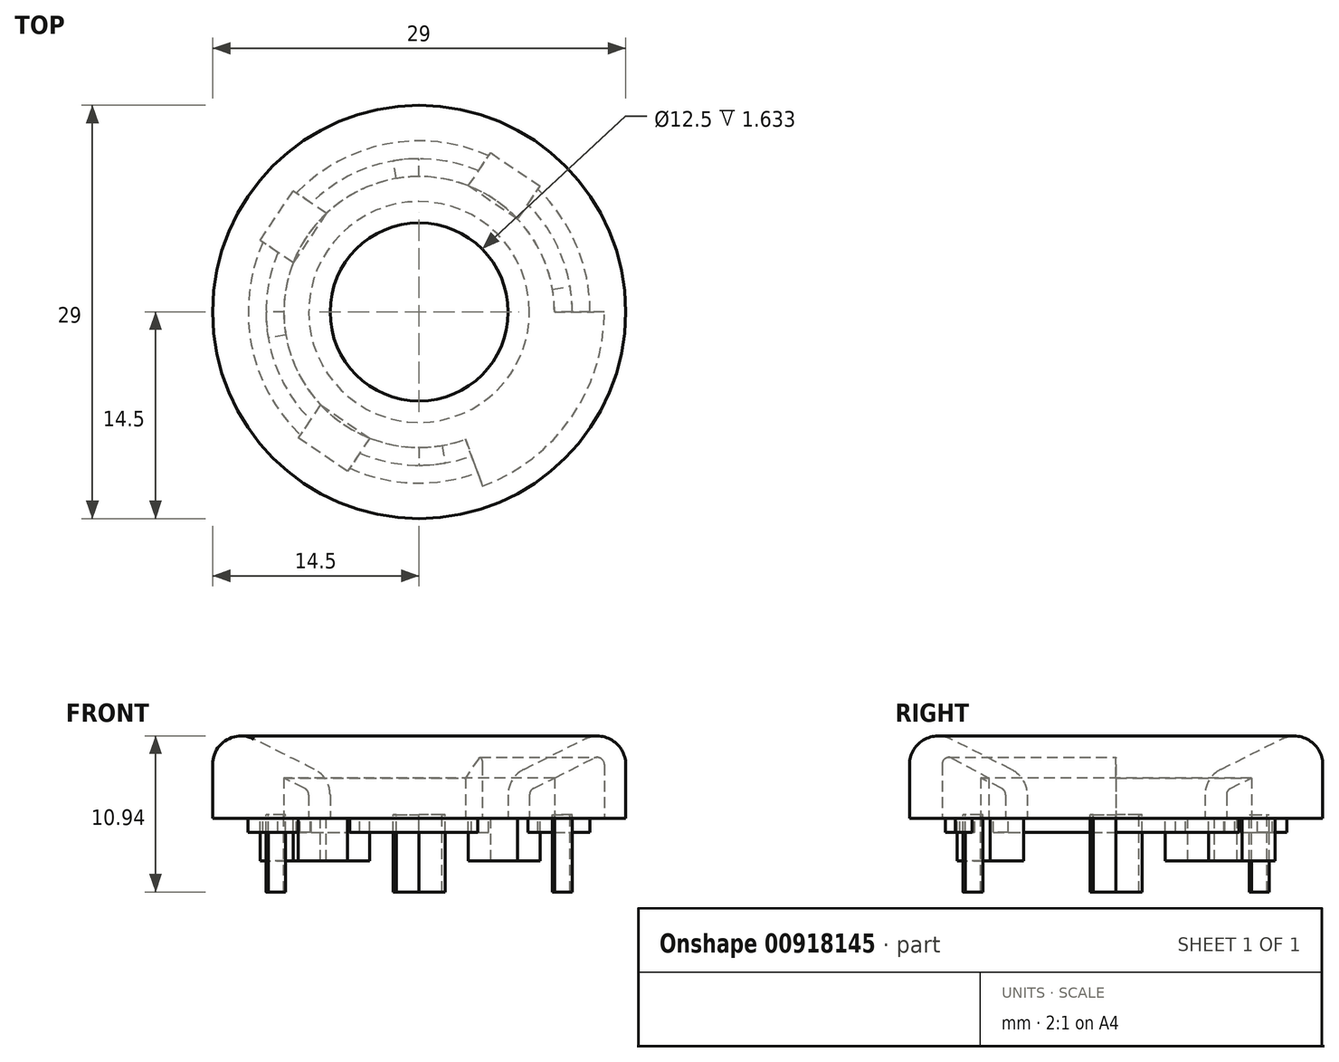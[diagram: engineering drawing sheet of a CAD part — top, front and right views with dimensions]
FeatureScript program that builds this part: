
annotation { "Feature Type Name" : "Feature", "Feature Type Description" : "" }
export const myFeature = defineFeature(function(context is Context, id is Id, definition is map)
    precondition{}
    {
        {
            var Q0;
            Q0=qCreatedBy(makeId("Front.planeOp"),FACE);
            var sketch = newSketch(context, id + "F0", { "sketchPlane" : qUnion([Q0])});
            skLineSegment(sketch, "E0", {"start": v(-6.25, 0) * mm, "end": v(-14.5, 0) * mm});
            skLineSegment(sketch, "E1", {"start": v(-14.5, 0) * mm, "end": v(-14.5, 3.76) * mm});
            skLineSegment(sketch, "E2", {"start": v(-6.25, 1.63) * mm, "end": v(-6.25, 0) * mm});
            skPoint(sketch, "E3.visualSharp", {"position": v(-14.5, 7) * mm});
            skPoint(sketch, "E4.orphan", {"position": v(0, 0) * mm});
            skPoint(sketch, "E5.visualSharp", {"position": v(-6.25, 2.47) * mm});
            skArc(sketch, "E5.filletArc", {"start": v(-6.25, 1.63) * mm, "mid": v(-6.55, 2.68) * mm, "end": v(-7.35, 3.42) * mm});
            skLineSegment(sketch, "E6", {"start": v(0, 0) * mm, "end": v(0, 11.37) * mm, "construction": true});
            skLineSegment(sketch, "E7", {"start": v(-7.35, 3.42) * mm, "end": v(-11.6, 5.55) * mm});
            skPoint(sketch, "E8.orphan", {"position": v(-14.5, 7.63) * mm});
            skArc(sketch, "E9.filletArc", {"start": v(-11.6, 5.55) * mm, "mid": v(-13.55, 5.46) * mm, "end": v(-14.5, 3.76) * mm});
            skSolve(sketch);
        }
        {
            var Q0;
            Q0=makeQuery(id+"F0.imprint","IMPRINT",FACE,{"disambiguationData":[TD([[makeQuery(id+"F0.imprint","IMPRINT",EDGE,{"derivedFrom":sQuery(id+"F0.wireOp",EDGE,"E0")}),-1.0]])]});
            var Q1;
            Q1=sQuery(id+"F0.wireOp",EDGE,"E6");
            revolve(context, id + "F1", {"surfaceOperationType" : NewSurfaceOperationType.NEW, "entities" : qUnion([Q0]), "axis" : qUnion([Q1]), "revolveType" : RevolveType.FULL});
        }
        {
            var Q0;
            Q0=makeQuery(id+"F1.opRevolve","SWEPT_FACE",FACE,{"disambiguationData":[OSD([sQuery(id+"F0.wireOp",EDGE,"E0")])]});
            shell(context, id + "F2", {"entities" : qUnion([Q0]), "thickness" : 1.5 * mm});
        }
        {
            var Q0;
            Q0=makeQuery(id+"F1.opRevolve","SWEPT_FACE",FACE,{"disambiguationData":[OSD([sQuery(id+"F0.wireOp",EDGE,"E0")])]});
            var sketch = newSketch(context, id + "F3", { "sketchPlane" : qUnion([Q0])});
            skLineSegment(sketch, "E10", {"start": v(13, 0) * mm, "end": v(9.5, 0) * mm});
            skArc(sketch, "E11", {"start": v(3.25, 8.93) * mm, "mid": v(-7.78, -5.45) * mm, "end": v(9.5, 0) * mm});
            skArc(sketch, "E12", {"start": v(4.45, 12.22) * mm, "mid": v(-10.65, -7.46) * mm, "end": v(13, 0) * mm});
            skLineSegment(sketch, "E13", {"start": v(3.25, 8.93) * mm, "end": v(4.45, 12.22) * mm});
            skPoint(sketch, "E14.orphan", {"position": v(0, 9.5) * mm});
            skSolve(sketch);
        }
        {
            var Q0;
            Q0=makeQuery(id+"F3.imprint","IMPRINT",FACE,{"disambiguationData":[TD([[makeQuery(id+"F3.imprint","IMPRINT",EDGE,{"derivedFrom":sQuery(id+"F3.wireOp",EDGE,"E10")}),1.0]])]});
            extrude(context, id + "F4", {"entities" : qUnion([Q0]), "operationType" : NewBodyOperationType.ADD, "endBound" : BoundingType.UP_TO_NEXT, "oppositeDirection" : true, "depth" : 25 * mm, "offsetDistance" : 25 * mm});
        }
        {
            var Q0;
            Q0=makeQuery(id+"F4.boolean.opBoolean","MERGE",FACE,{"derivedFrom":[makeQuery(id+"F1.opRevolve","SWEPT_FACE",FACE,{"disambiguationData":[OSD([sQuery(id+"F0.wireOp",EDGE,"E0")])]}),makeQuery(id+"F4.opExtrude","CAP_FACE",FACE,{"disambiguationData":[OSD([sQuery(id+"F3.wireOp",EDGE,"E10"),sQuery(id+"F3.wireOp",EDGE,"E11"),sQuery(id+"F3.wireOp",EDGE,"E12"),sQuery(id+"F3.wireOp",EDGE,"E13")])],"isStart":true})]});
            var sketch = newSketch(context, id + "F5", { "sketchPlane" : qUnion([Q0])});
            skLineSegment(sketch, "E15", {"start": v(6.92, -6.5) * mm, "end": v(3.46, -8.85) * mm});
            skLineSegment(sketch, "E16", {"start": v(3.46, -8.85) * mm, "end": v(5.03, -11.17) * mm});
            skLineSegment(sketch, "E17", {"start": v(5.03, -11.17) * mm, "end": v(8.49, -8.83) * mm});
            skLineSegment(sketch, "E18", {"start": v(6.92, -6.5) * mm, "end": v(8.49, -8.83) * mm});
            skLineSegment(sketch, "E19.1.0", {"start": v(-6.5, -6.92) * mm, "end": v(-8.83, -8.49) * mm});
            skLineSegment(sketch, "E19.1.1", {"start": v(-6.5, -6.92) * mm, "end": v(-8.85, -3.46) * mm});
            skLineSegment(sketch, "E19.1.2", {"start": v(-11.17, -5.03) * mm, "end": v(-8.83, -8.49) * mm});
            skLineSegment(sketch, "E19.1.3", {"start": v(-8.85, -3.46) * mm, "end": v(-11.17, -5.03) * mm});
            skLineSegment(sketch, "E19.2.0", {"start": v(-6.92, 6.5) * mm, "end": v(-8.49, 8.83) * mm});
            skLineSegment(sketch, "E19.2.1", {"start": v(-6.92, 6.5) * mm, "end": v(-3.46, 8.85) * mm});
            skLineSegment(sketch, "E19.2.2", {"start": v(-5.03, 11.17) * mm, "end": v(-8.49, 8.83) * mm});
            skLineSegment(sketch, "E19.2.3", {"start": v(-3.46, 8.85) * mm, "end": v(-5.03, 11.17) * mm});
            skPoint(sketch, "E19.center", {"position": v(0, 0) * mm});
            skLineSegment(sketch, "E19.anchor1", {"start": v(0, 0) * mm, "end": v(5.03, -11.17) * mm, "construction": true});
            skLineSegment(sketch, "E19.anchor2", {"start": v(0, 0) * mm, "end": v(-5.03, 11.17) * mm, "construction": true});
            skSolve(sketch);
        }
        {
            var Q0;
            {var subQ0=sQuery(id+"F5.wireOp",EDGE,"E19.2.0");Q0=makeQuery(id+"F5.imprint","IMPRINT",FACE,{"disambiguationData":[TD([[makeQuery(id+"F5.imprint","IMPRINT",EDGE,{"derivedFrom":subQ0}),-1.0]])]});}
            var Q1;
            {var subQ0=sQuery(id+"F5.wireOp",EDGE,"E19.1.0");Q1=makeQuery(id+"F5.imprint","IMPRINT",FACE,{"disambiguationData":[TD([[makeQuery(id+"F5.imprint","IMPRINT",EDGE,{"derivedFrom":subQ0}),-1.0]])]});}
            var Q2;
            {var subQ0=sQuery(id+"F5.wireOp",EDGE,"E16");Q2=makeQuery(id+"F5.imprint","IMPRINT",FACE,{"disambiguationData":[TD([[makeQuery(id+"F5.imprint","IMPRINT",EDGE,{"derivedFrom":subQ0}),1.0]])]});}
            var Q3;
            {var subQ0=sQuery(id+"F5.wireOp",EDGE,"E15");Q3=makeQuery(id+"F5.imprint","IMPRINT",FACE,{"disambiguationData":[TD([[makeQuery(id+"F5.imprint","IMPRINT",EDGE,{"derivedFrom":subQ0}),1.0]])]});}
            var Q4;
            {var subQ0=sQuery(id+"F5.wireOp",EDGE,"E19.1.1");Q4=makeQuery(id+"F5.imprint","IMPRINT",FACE,{"disambiguationData":[TD([[makeQuery(id+"F5.imprint","IMPRINT",EDGE,{"derivedFrom":subQ0}),1.0]])]});}
            var Q5;
            {var subQ0=sQuery(id+"F5.wireOp",EDGE,"E19.2.1");Q5=makeQuery(id+"F5.imprint","IMPRINT",FACE,{"disambiguationData":[TD([[makeQuery(id+"F5.imprint","IMPRINT",EDGE,{"derivedFrom":subQ0}),1.0]])]});}
            extrude(context, id + "F6", {"entities" : qUnion([Q0, Q1, Q2, Q3, Q4, Q5]), "operationType" : NewBodyOperationType.ADD, "depth" : 3 * mm, "offsetDistance" : 25 * mm});
        }
        {
            var Q0;
            Q0=makeQuery(id+"F4.boolean.opBoolean","MERGE",FACE,{"derivedFrom":[makeQuery(id+"F1.opRevolve","SWEPT_FACE",FACE,{"disambiguationData":[OSD([sQuery(id+"F0.wireOp",EDGE,"E0")])]}),makeQuery(id+"F4.opExtrude","CAP_FACE",FACE,{"disambiguationData":[OSD([sQuery(id+"F3.wireOp",EDGE,"E10"),sQuery(id+"F3.wireOp",EDGE,"E11"),sQuery(id+"F3.wireOp",EDGE,"E12"),sQuery(id+"F3.wireOp",EDGE,"E13")])],"isStart":true})]});
            var sketch = newSketch(context, id + "F7", { "sketchPlane" : qUnion([Q0])});
            skArc(sketch, "E20", {"start": v(4.1, 11.28) * mm, "mid": v(-9.83, -6.88) * mm, "end": v(12, 0) * mm});
            skArc(sketch, "E21", {"start": v(3.68, 10.1) * mm, "mid": v(-8.8, -6.17) * mm, "end": v(10.75, 0) * mm});
            skLineSegment(sketch, "E22", {"start": v(3.68, 10.1) * mm, "end": v(4.1, 11.28) * mm});
            skLineSegment(sketch, "E23", {"start": v(9.5, 0) * mm, "end": v(12, 0) * mm});
            skSolve(sketch);
        }
        {
            var Q0;
            Q0 = qSketchRegion(id + "F7", true);
            extrude(context, id + "F8", {"entities" : qUnion([Q0]), "operationType" : NewBodyOperationType.ADD, "depth" : 1 * mm, "offsetDistance" : 25 * mm});
        }
        {
            var Q0;
            {var subQ0=sQuery(id+"F5.wireOp",EDGE,"E15");var subQ1=sQuery(id+"F3.wireOp",EDGE,"E11");var subQ2=sQuery(id+"F5.wireOp",EDGE,"E18");var subQ3=sQuery(id+"F3.wireOp",EDGE,"E10");Q0=makeQuery(id+"F8.boolean.opBoolean","SPLIT",FACE,{"disambiguationData":[TD([makeQuery(id+"F4.opExtrude","SWEPT_FACE",FACE,{"disambiguationData":[OSD([subQ3])]}),makeQuery(id+"F4.opExtrude","SWEPT_FACE",FACE,{"disambiguationData":[OSD([subQ1])]}),makeQuery(id+"F6.opExtrude","SWEPT_FACE",FACE,{"disambiguationData":[OSD([subQ0])]}),makeQuery(id+"F6.opExtrude","CAP_FACE",FACE,{"disambiguationData":[OSD([subQ0,sQuery(id+"F5.wireOp",EDGE,"E16"),sQuery(id+"F5.wireOp",EDGE,"E17"),subQ2])],"isStart":true}),makeQuery(id+"F6.opExtrude","SWEPT_FACE",FACE,{"disambiguationData":[OSD([subQ2])]}),makeQuery(id+"F8.opExtrude","SWEPT_FACE",FACE,{"disambiguationData":[OSD([sQuery(id+"F7.wireOp",EDGE,"E21")])]}),makeQuery(id+"F8.opExtrude","SWEPT_FACE",FACE,{"disambiguationData":[OSD([sQuery(id+"F7.wireOp",EDGE,"E23")])]})])],"derivedFrom":makeQuery(id+"F4.boolean.opBoolean","MERGE",FACE,{"derivedFrom":[makeQuery(id+"F1.opRevolve","SWEPT_FACE",FACE,{"disambiguationData":[OSD([sQuery(id+"F0.wireOp",EDGE,"E0")])]}),makeQuery(id+"F4.opExtrude","CAP_FACE",FACE,{"disambiguationData":[OSD([subQ3,subQ1,sQuery(id+"F3.wireOp",EDGE,"E12"),sQuery(id+"F3.wireOp",EDGE,"E13")])],"isStart":true})]})});}
            var sketch = newSketch(context, id + "F9", { "sketchPlane" : qUnion([Q0])});
            skLineSegment(sketch, "E24", {"start": v(9.5, 0) * mm, "end": v(10.75, 0) * mm});
            skLineSegment(sketch, "E25", {"start": v(9.36, -1.6) * mm, "end": v(10.6, -1.81) * mm});
            skArc(sketch, "E26", {"start": v(9.5, 0) * mm, "mid": v(9.47, -0.8) * mm, "end": v(9.36, -1.6) * mm});
            skArc(sketch, "E27", {"start": v(10.75, 0) * mm, "mid": v(10.71, -0.91) * mm, "end": v(10.6, -1.81) * mm});
            skLineSegment(sketch, "E28.1.0", {"start": v(0, 9.5) * mm, "end": v(0, 10.75) * mm});
            skArc(sketch, "E28.1.1", {"start": v(0, 10.75) * mm, "mid": v(0.91, 10.71) * mm, "end": v(1.81, 10.6) * mm});
            skLineSegment(sketch, "E28.1.2", {"start": v(1.6, 9.36) * mm, "end": v(1.81, 10.6) * mm});
            skArc(sketch, "E28.1.3", {"start": v(0, 9.5) * mm, "mid": v(0.8, 9.47) * mm, "end": v(1.6, 9.36) * mm});
            skLineSegment(sketch, "E28.2.0", {"start": v(-9.5, 0) * mm, "end": v(-10.75, 0) * mm});
            skArc(sketch, "E28.2.1", {"start": v(-10.75, 0) * mm, "mid": v(-10.71, 0.91) * mm, "end": v(-10.6, 1.81) * mm});
            skLineSegment(sketch, "E28.2.2", {"start": v(-9.36, 1.6) * mm, "end": v(-10.6, 1.81) * mm});
            skArc(sketch, "E28.2.3", {"start": v(-9.5, 0) * mm, "mid": v(-9.47, 0.8) * mm, "end": v(-9.36, 1.6) * mm});
            skLineSegment(sketch, "E28.3.0", {"start": v(0, -9.5) * mm, "end": v(0, -10.75) * mm});
            skArc(sketch, "E28.3.1", {"start": v(0, -10.75) * mm, "mid": v(-0.91, -10.71) * mm, "end": v(-1.81, -10.6) * mm});
            skLineSegment(sketch, "E28.3.2", {"start": v(-1.6, -9.36) * mm, "end": v(-1.81, -10.6) * mm});
            skArc(sketch, "E28.3.3", {"start": v(0, -9.5) * mm, "mid": v(-0.8, -9.47) * mm, "end": v(-1.6, -9.36) * mm});
            skSolve(sketch);
        }
        {
            var Q0;
            Q0=makeQuery(id+"F9.imprint","IMPRINT",FACE,{"disambiguationData":[TD([[makeQuery(id+"F9.imprint","IMPRINT",EDGE,{"derivedFrom":sQuery(id+"F9.wireOp",EDGE,"E28.1.0")}),-1.0]])]});
            var Q1;
            Q1=makeQuery(id+"F9.imprint","IMPRINT",FACE,{"disambiguationData":[TD([[makeQuery(id+"F9.imprint","IMPRINT",EDGE,{"derivedFrom":sQuery(id+"F9.wireOp",EDGE,"E24")}),1.0]])]});
            var Q2;
            Q2=makeQuery(id+"F9.imprint","IMPRINT",FACE,{"disambiguationData":[TD([[makeQuery(id+"F9.imprint","IMPRINT",EDGE,{"derivedFrom":sQuery(id+"F9.wireOp",EDGE,"E28.3.0")}),-1.0]])]});
            var Q3;
            Q3=makeQuery(id+"F9.imprint","IMPRINT",FACE,{"disambiguationData":[TD([[makeQuery(id+"F9.imprint","IMPRINT",EDGE,{"derivedFrom":sQuery(id+"F9.wireOp",EDGE,"E28.2.0")}),-1.0]])]});
            extrude(context, id + "F10", {"entities" : qUnion([Q0, Q1, Q2, Q3]), "depth" : 5.18 * mm, "offsetDistance" : 25 * mm, "hasSecondDirection" : true, "secondDirectionOppositeDirection" : true, "secondDirectionDepth" : .25 * mm});
        }
    });
